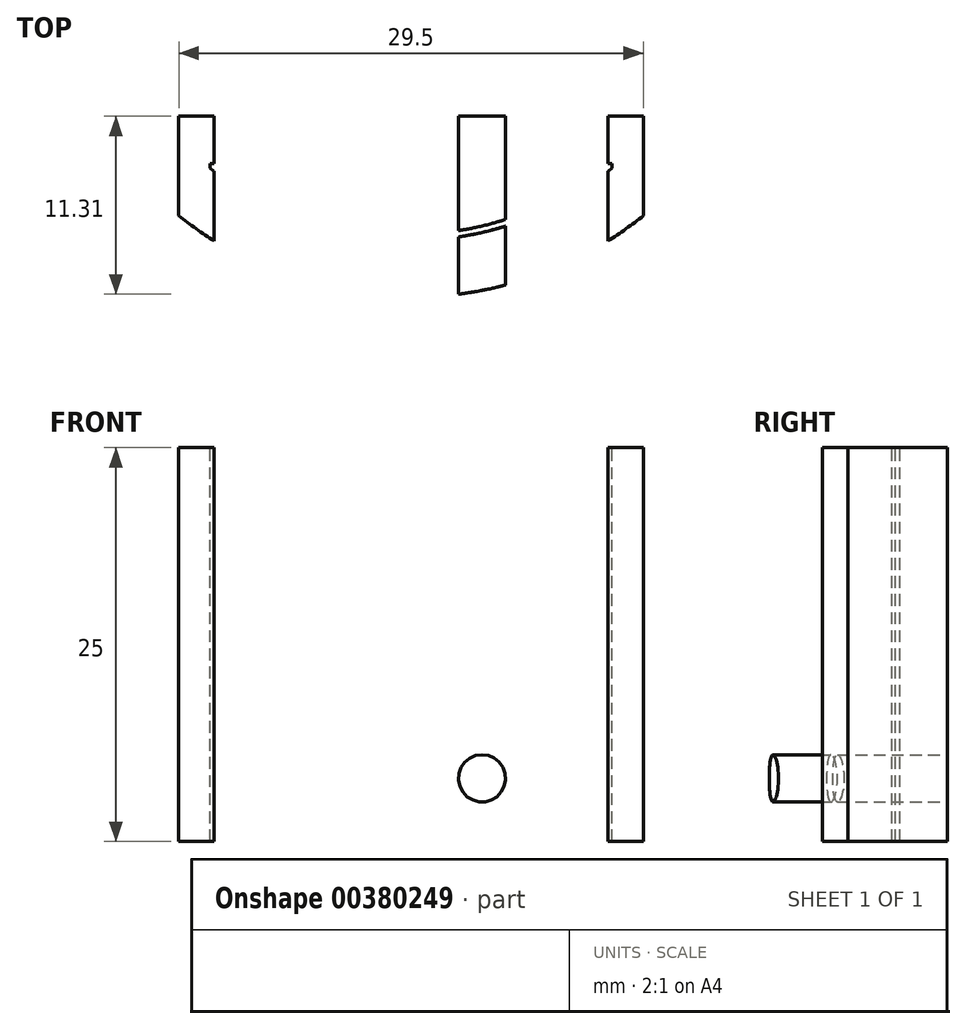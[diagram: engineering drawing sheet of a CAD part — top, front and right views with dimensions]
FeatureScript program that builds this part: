
annotation { "Feature Type Name" : "Feature", "Feature Type Description" : "" }
export const myFeature = defineFeature(function(context is Context, id is Id, definition is map)
    precondition{}
    {
        {
            var Q0;
            Q0=qCreatedBy(makeId("Top.planeOp"),FACE);
            var sketch = newSketch(context, id + "F0", { "sketchPlane" : qUnion([Q0])});
            skLineSegment(sketch, "E0", {"start": v(0, 0) * mm, "end": v(25, 0) * mm});
            skArc(sketch, "E1", {"start": v(0, 0) * mm, "mid": v(12.5, -4.5) * mm, "end": v(25, 0) * mm});
            skLineSegment(sketch, "E2.top", {"start": v(0, 3) * mm, "end": v(25, 3) * mm});
            skLineSegment(sketch, "E2.left", {"start": v(0, 0) * mm, "end": v(0, 3) * mm});
            skLineSegment(sketch, "E2.right", {"start": v(25, 0) * mm, "end": v(25, 3) * mm});
            skSolve(sketch);
        }
        {
            var Q0;
            Q0=makeQuery(id+"F0.imprint","IMPRINT",FACE,{"disambiguationData":[TD([[makeQuery(id+"F0.imprint","IMPRINT",EDGE,{"derivedFrom":sQuery(id+"F0.wireOp",EDGE,"E0")}),1.0]])]});
            var Q1;
            Q1=makeQuery(id+"F0.imprint","IMPRINT",FACE,{"disambiguationData":[TD([[makeQuery(id+"F0.imprint","IMPRINT",EDGE,{"derivedFrom":sQuery(id+"F0.wireOp",EDGE,"E1")}),1.0]])]});
            extrude(context, id + "F1", {"entities" : qUnion([Q0, Q1]), "depth" : 25 * mm});
        }
        {
            var Q0;
            Q0=makeQuery(id+"F1.opExtrude","CAP_FACE",FACE,{"disambiguationData":[OSD([sQuery(id+"F0.wireOp",EDGE,"E1"),sQuery(id+"F0.wireOp",EDGE,"E2.top"),sQuery(id+"F0.wireOp",EDGE,"E2.left"),sQuery(id+"F0.wireOp",EDGE,"E2.right")])],"isStart":false});
            var sketch = newSketch(context, id + "F2", { "sketchPlane" : qUnion([Q0])});
            skArc(sketch, "E3.0", {"start": v(-0.25, -0.3) * mm, "mid": v(12.5, -4.9) * mm, "end": v(25.25, -0.3) * mm});
            skLineSegment(sketch, "E4", {"start": v(-0.25, -0.3) * mm, "end": v(-2.25, -0.3) * mm});
            skLineSegment(sketch, "E5", {"start": v(-2.25, -0.3) * mm, "end": v(-2.25, 3) * mm});
            skLineSegment(sketch, "E6", {"start": v(0, 3) * mm, "end": v(-2.25, 3) * mm});
            skLineSegment(sketch, "E7", {"start": v(-0.25, -0.3) * mm, "end": v(-0.25, 0) * mm});
            skLineSegment(sketch, "E8", {"start": v(-0.25, 0) * mm, "end": v(0, 0) * mm});
            skArc(sketch, "E9.0", {"start": v(-2.25, -3.32) * mm, "mid": v(12.5, -8.5) * mm, "end": v(27.25, -3.32) * mm});
            skLineSegment(sketch, "E10", {"start": v(-2.25, -0.3) * mm, "end": v(-2.25, -3.32) * mm});
            skLineSegment(sketch, "E11.MirrorCS", {"start": v(25.25, 0) * mm, "end": v(25, 0) * mm});
            skLineSegment(sketch, "E12.MirrorCS", {"start": v(25.25, -0.3) * mm, "end": v(25.25, 0) * mm});
            skLineSegment(sketch, "E13.MirrorCS", {"start": v(25.25, -0.3) * mm, "end": v(27.25, -0.3) * mm});
            skLineSegment(sketch, "E14.MirrorCS", {"start": v(27.25, -0.3) * mm, "end": v(27.25, 3) * mm});
            skLineSegment(sketch, "E15.MirrorCS", {"start": v(27.25, -0.3) * mm, "end": v(27.25, -3.32) * mm});
            skLineSegment(sketch, "E16.MirrorCS", {"start": v(25, 3) * mm, "end": v(27.25, 3) * mm});
            skSolve(sketch);
        }
        {
            var Q0;
            Q0=makeQuery(id+"F2.imprint","IMPRINT",FACE,{"disambiguationData":[TD([[makeQuery(id+"F2.imprint","IMPRINT",EDGE,{"derivedFrom":sQuery(id+"F2.wireOp",EDGE,"E4")}),-1.0]])]});
            var Q1;
            Q1=makeQuery(id+"F2.imprint","IMPRINT",FACE,{"disambiguationData":[TD([[makeQuery(id+"F2.imprint","IMPRINT",EDGE,{"derivedFrom":sQuery(id+"F2.wireOp",EDGE,"E3.0")}),-1.0]])]});
            var Q2;
            Q2=makeQuery(id+"F2.imprint","IMPRINT",FACE,{"disambiguationData":[TD([[makeQuery(id+"F2.imprint","IMPRINT",EDGE,{"derivedFrom":sQuery(id+"F2.wireOp",EDGE,"E11.MirrorCS")}),-1.0]])]});
            extrude(context, id + "F3", {"entities" : qUnion([Q0, Q1, Q2]), "oppositeDirection" : true, "depth" : 25 * mm});
        }
        {
            var Q0;
            Q0=makeQuery(id+"F1.opExtrude","SWEPT_FACE",FACE,{"disambiguationData":[OSD([sQuery(id+"F0.wireOp",EDGE,"E2.top")])]});
            var sketch = newSketch(context, id + "F4", { "sketchPlane" : qUnion([Q0])});
            skCircle(sketch, "E17", {"center": v(-8, 4) * mm, "radius": 1.5 * mm});
            skCircle(sketch, "E18.MirrorC", {"center": v(-17, 4) * mm, "radius": 1.5 * mm});
            skSolve(sketch);
        }
        {
            var Q0;
            Q0=makeQuery(id+"F4.imprint","IMPRINT",FACE,{"disambiguationData":[TD([[makeQuery(id+"F4.imprint","IMPRINT",EDGE,{"derivedFrom":sQuery(id+"F4.wireOp",EDGE,"E18.MirrorC")}),-1.0]])]});
            var Q1;
            Q1=makeQuery(id+"F4.imprint","IMPRINT",FACE,{"disambiguationData":[TD([[makeQuery(id+"F4.imprint","IMPRINT",EDGE,{"derivedFrom":sQuery(id+"F4.wireOp",EDGE,"E17")}),1.0]])]});
            extrude(context, id + "F5", {"entities" : qUnion([Q0, Q1]), "operationType" : NewBodyOperationType.REMOVE, "oppositeDirection" : true, "depth" : 25 * mm});
        }
        {
            var Q0;
            Q0=makeQuery(id+"F3.opExtrude","SWEPT_BODY",BODY,{"disambiguationData":[OSD([sQuery(id+"F0.wireOp",EDGE,"E2.left"),sQuery(id+"F0.wireOp",EDGE,"E2.right"),sQuery(id+"F2.wireOp",EDGE,"E3.0"),sQuery(id+"F2.wireOp",EDGE,"E5"),sQuery(id+"F2.wireOp",EDGE,"E6"),sQuery(id+"F2.wireOp",EDGE,"E7"),sQuery(id+"F2.wireOp",EDGE,"E8"),sQuery(id+"F2.wireOp",EDGE,"E9.0"),sQuery(id+"F2.wireOp",EDGE,"E10"),sQuery(id+"F2.wireOp",EDGE,"E11.MirrorCS"),sQuery(id+"F2.wireOp",EDGE,"E12.MirrorCS"),sQuery(id+"F2.wireOp",EDGE,"E14.MirrorCS"),sQuery(id+"F2.wireOp",EDGE,"E15.MirrorCS"),sQuery(id+"F2.wireOp",EDGE,"E16.MirrorCS")])]});
            var Q1;
            Q1=makeQuery(id+"F1.opExtrude","SWEPT_BODY",BODY,{"disambiguationData":[OSD([sQuery(id+"F0.wireOp",EDGE,"E1"),sQuery(id+"F0.wireOp",EDGE,"E2.top"),sQuery(id+"F0.wireOp",EDGE,"E2.left"),sQuery(id+"F0.wireOp",EDGE,"E2.right")])]});
            booleanBodies(context, id + "F6", {"operationType" : BooleanOperationType.UNION, "tools" : qUnion([Q0, Q1])});
        }
        {
            var Q0;
            {var subQ0=sQuery(id+"F0.wireOp",EDGE,"E2.right");var subQ1=sQuery(id+"F0.wireOp",EDGE,"E2.left");Q0=makeQuery(id+"F6.opBoolean","MERGE",FACE,{"derivedFrom":[makeQuery(id+"F1.opExtrude","CAP_FACE",FACE,{"disambiguationData":[OSD([sQuery(id+"F0.wireOp",EDGE,"E1"),sQuery(id+"F0.wireOp",EDGE,"E2.top"),subQ1,subQ0])],"isStart":true}),makeQuery(id+"F3.opExtrude","CAP_FACE",FACE,{"disambiguationData":[OSD([subQ1,subQ0,sQuery(id+"F2.wireOp",EDGE,"E3.0"),sQuery(id+"F2.wireOp",EDGE,"E5"),sQuery(id+"F2.wireOp",EDGE,"E6"),sQuery(id+"F2.wireOp",EDGE,"E7"),sQuery(id+"F2.wireOp",EDGE,"E8"),sQuery(id+"F2.wireOp",EDGE,"E9.0"),sQuery(id+"F2.wireOp",EDGE,"E10"),sQuery(id+"F2.wireOp",EDGE,"E11.MirrorCS"),sQuery(id+"F2.wireOp",EDGE,"E12.MirrorCS"),sQuery(id+"F2.wireOp",EDGE,"E14.MirrorCS"),sQuery(id+"F2.wireOp",EDGE,"E15.MirrorCS"),sQuery(id+"F2.wireOp",EDGE,"E16.MirrorCS")])],"isStart":false})]});}
            var sketch = newSketch(context, id + "F7", { "sketchPlane" : qUnion([Q0])});
            skLineSegment(sketch, "E19", {"start": v(12.5, -3) * mm, "end": v(12.5, 0) * mm});
            skLineSegment(sketch, "E20.0", {"start": v(15.5, -3) * mm, "end": v(18.5, -3) * mm});
            skLineSegment(sketch, "E21.0", {"start": v(9.5, -3) * mm, "end": v(6.5, -3) * mm});
            skArc(sketch, "E22", {"start": v(15.5, -3) * mm, "mid": v(12.5, 0) * mm, "end": v(9.5, -3) * mm});
            skLineSegment(sketch, "E23", {"start": v(15.5, -3) * mm, "end": v(9.5, -3) * mm});
            skSolve(sketch);
        }
        {
            var Q0;
            {var subQ0=sQuery(id+"F7.wireOp",EDGE,"E19");Q0=makeQuery(id+"F7.imprint","IMPRINT",FACE,{"disambiguationData":[TD([[makeQuery(id+"F7.imprint","IMPRINT",EDGE,{"derivedFrom":subQ0}),-1.0]])]});}
            var Q1;
            {var subQ0=sQuery(id+"F7.wireOp",EDGE,"E19");Q1=makeQuery(id+"F7.imprint","IMPRINT",FACE,{"disambiguationData":[TD([[makeQuery(id+"F7.imprint","IMPRINT",EDGE,{"derivedFrom":subQ0}),1.0]])]});}
            extrude(context, id + "F8", {"entities" : qUnion([Q0, Q1]), "operationType" : NewBodyOperationType.REMOVE, "oppositeDirection" : true, "depth" : 25 * mm});
        }
    });
